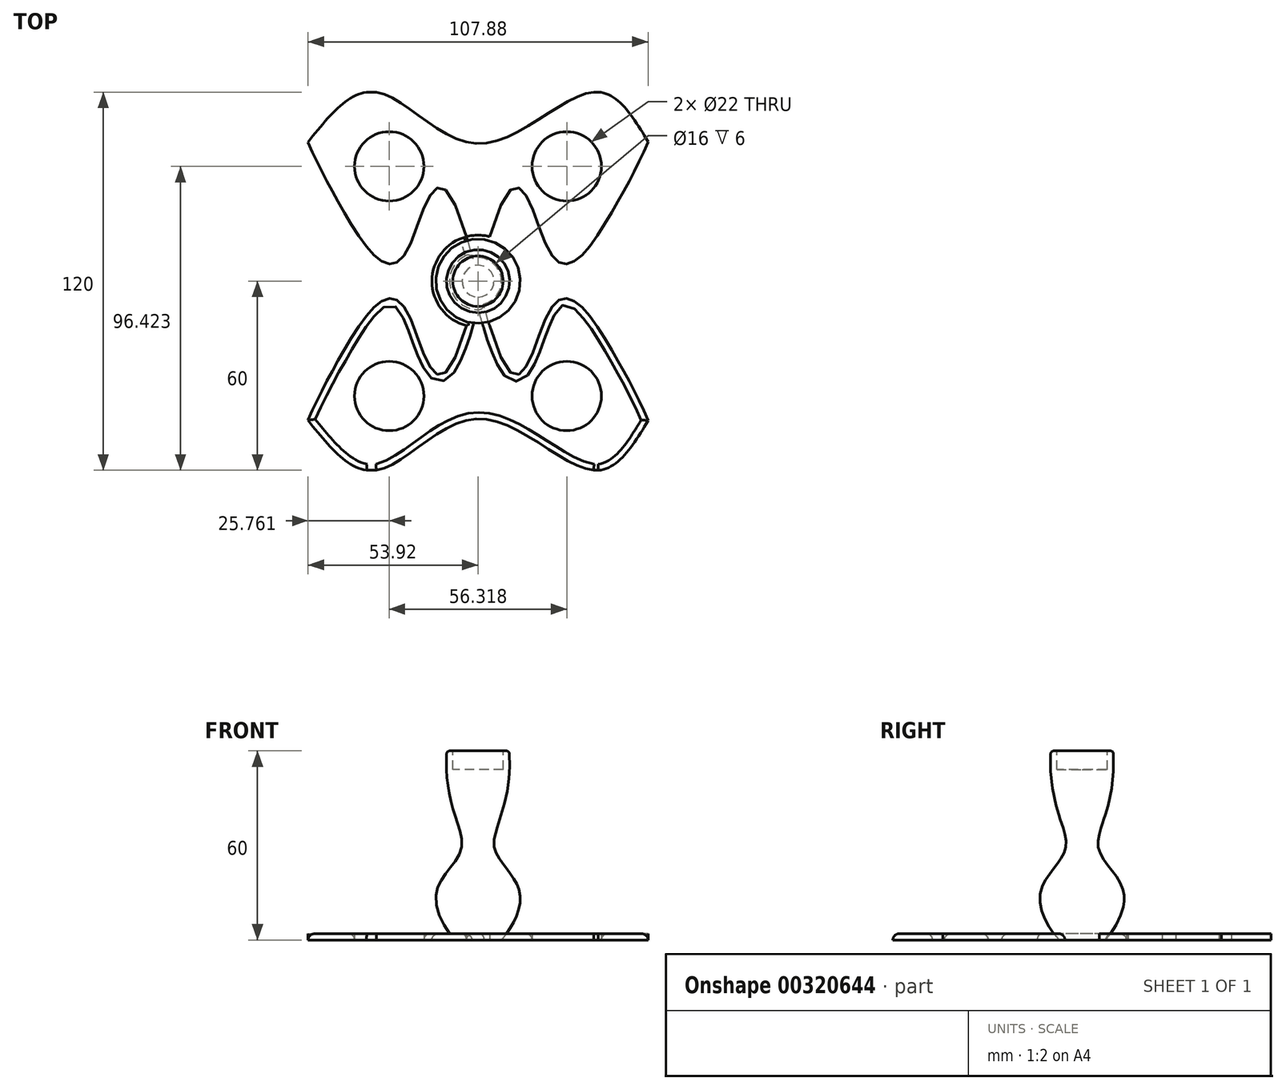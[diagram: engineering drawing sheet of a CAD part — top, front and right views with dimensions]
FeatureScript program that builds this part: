
annotation { "Feature Type Name" : "Feature", "Feature Type Description" : "" }
export const myFeature = defineFeature(function(context is Context, id is Id, definition is map)
    precondition{}
    {
        {
            var Q0;
            Q0=qCreatedBy(makeId("Top.planeOp"),FACE);
            var sketch = newSketch(context, id + "F0", { "sketchPlane" : qUnion([Q0])});
            skLineSegment(sketch, "E0.bottom", {"start": v(60, -60) * mm, "end": v(-60, -60) * mm});
            skLineSegment(sketch, "E0.top", {"start": v(60, 60) * mm, "end": v(-60, 60) * mm});
            skLineSegment(sketch, "E0.left", {"start": v(60, -60) * mm, "end": v(60, 60) * mm});
            skLineSegment(sketch, "E0.right", {"start": v(-60, -60) * mm, "end": v(-60, 60) * mm});
            skPoint(sketch, "E0.middle", {"position": v(0, 0) * mm});
            skCircle(sketch, "E1", {"center": v(-28.16, 36.42) * mm, "radius": 11 * mm});
            skCircle(sketch, "E2.MirrorC", {"center": v(28.16, 36.42) * mm, "radius": 11 * mm});
            skCircle(sketch, "E3.MirrorC", {"center": v(28.16, -36.42) * mm, "radius": 11 * mm});
            skCircle(sketch, "E4.MirrorC", {"center": v(-28.16, -36.42) * mm, "radius": 11 * mm});
            skFitSpline(sketch, "E5", {"points": [v(-60, 60) * mm, v(-42.49, 21.96) * mm, v(-22.78, 9.17) * mm, v(0, 0) * mm], "startDerivative": vector(42.96, -123.6) * mm, "endDerivative": vector(125.1, -535.95) * mm});
            skFitSpline(sketch, "E6.MirrorCS", {"points": [v(60, 60) * mm, v(42.49, 21.96) * mm, v(22.78, 9.17) * mm, v(0, 0) * mm], "startDerivative": vector(-42.96, -123.6) * mm, "endDerivative": vector(-125.1, -535.95) * mm});
            skFitSpline(sketch, "E7.MirrorCS", {"points": [v(-60, -60) * mm, v(-42.49, -21.96) * mm, v(-22.78, -9.17) * mm, v(0, 0) * mm], "startDerivative": vector(42.96, 123.6) * mm, "endDerivative": vector(125.1, 535.95) * mm});
            skFitSpline(sketch, "E8.MirrorCS", {"points": [v(60, -60) * mm, v(42.49, -21.96) * mm, v(22.78, -9.17) * mm, v(0, 0) * mm], "startDerivative": vector(-42.96, 123.6) * mm, "endDerivative": vector(-125.1, 535.95) * mm});
            skCircle(sketch, "E9", {"center": v(0, 0) * mm, "radius": 14.6 * mm});
            skFitSpline(sketch, "E10", {"points": [v(-54.3, -43.62) * mm, v(-32.24, -60) * mm, v(0, -43.62) * mm, v(36.74, -60) * mm, v(54.3, -43.62) * mm], "startDerivative": vector(89.76, -113.6) * mm, "endDerivative": vector(68.72, 116.74) * mm});
            skFitSpline(sketch, "E11.MirrorCS", {"points": [v(-54.3, 43.62) * mm, v(-32.24, 60) * mm, v(0, 43.62) * mm, v(36.74, 60) * mm, v(54.3, 43.62) * mm], "startDerivative": vector(89.76, 113.6) * mm, "endDerivative": vector(68.72, -116.74) * mm});
            skSolve(sketch);
        }
        {
            var Q0;
            {var subQ2=sQuery(id+"F0.wireOp",EDGE,"E7.MirrorCS");var subQ5=sQuery(id+"F0.wireOp",EDGE,"E8.MirrorCS");var subQ6=makeQuery(id+"F0.imprint","INTERSECT",VERTEX,{"derivedFrom":[subQ2,subQ5]});Q0=makeQuery(id+"F0.imprint","IMPRINT",FACE,{"disambiguationData":[TD([[makeQuery(id+"F0.imprint","IMPRINT",EDGE,{"disambiguationData":[TD([[subQ6,1.0]])],"derivedFrom":subQ2}),1.0]])]});}
            var Q1;
            {var subQ0=sQuery(id+"F0.wireOp",EDGE,"E8.MirrorCS");var subQ1=sQuery(id+"F0.wireOp",EDGE,"E7.MirrorCS");var subQ2=makeQuery(id+"F0.imprint","INTERSECT",VERTEX,{"derivedFrom":[subQ1,subQ0]});Q1=makeQuery(id+"F0.imprint","IMPRINT",FACE,{"disambiguationData":[TD([[makeQuery(id+"F0.imprint","IMPRINT",EDGE,{"disambiguationData":[TD([[subQ2,1.0]])],"derivedFrom":subQ1}),-1.0]])]});}
            var Q2;
            Q2=makeQuery(id+"F0.imprint","IMPRINT",FACE,{"disambiguationData":[TD([[makeQuery(id+"F0.imprint","IMPRINT",EDGE,{"derivedFrom":sQuery(id+"F0.wireOp",EDGE,"E1")}),-1.0]])]});
            var Q3;
            Q3=makeQuery(id+"F0.imprint","IMPRINT",FACE,{"disambiguationData":[TD([[makeQuery(id+"F0.imprint","IMPRINT",EDGE,{"derivedFrom":sQuery(id+"F0.wireOp",EDGE,"E3.MirrorC")}),-1.0]])]});
            extrude(context, id + "F1", {"entities" : qUnion([Q0, Q1, Q2, Q3]), "depth" : 2 * mm});
        }
        {
            var Q0;
            Q0=makeQuery(id+"F1.opExtrude","CAP_FACE",FACE,{"disambiguationData":[OSD([sQuery(id+"F0.wireOp",EDGE,"E0.bottom"),sQuery(id+"F0.wireOp",EDGE,"E0.top"),sQuery(id+"F0.wireOp",EDGE,"E1"),sQuery(id+"F0.wireOp",EDGE,"E2.MirrorC"),sQuery(id+"F0.wireOp",EDGE,"E3.MirrorC"),sQuery(id+"F0.wireOp",EDGE,"E4.MirrorC"),sQuery(id+"F0.wireOp",EDGE,"E5"),sQuery(id+"F0.wireOp",EDGE,"E6.MirrorCS"),sQuery(id+"F0.wireOp",EDGE,"E7.MirrorCS"),sQuery(id+"F0.wireOp",EDGE,"E8.MirrorCS"),sQuery(id+"F0.wireOp",EDGE,"E9")])],"isStart":false});
            fillet(context, id + "F2", {"entities" : qUnion([Q0]), "radius" : 2 * mm, "tangentPropagation" : true, "allowEdgeOverflow" : false});
        }
        {
            var Q0;
            Q0=qCreatedBy(makeId("Right.planeOp"),FACE);
            var sketch = newSketch(context, id + "F3", { "sketchPlane" : qUnion([Q0])});
            skLineSegment(sketch, "E12", {"start": v(-9.92, 60) * mm, "end": v(0, 60) * mm});
            skLineSegment(sketch, "E13", {"start": v(0, 60) * mm, "end": v(0, 0) * mm});
            skPoint(sketch, "E14", {"position": v(-4.96, 60) * mm});
            skPoint(sketch, "E15", {"position": v(-7.43, 0) * mm});
            skFitSpline(sketch, "E16", {"points": [v(-9.92, 60) * mm, v(-5.26, 28.95) * mm, v(-12.97, 16) * mm, v(-7.43, 0) * mm], "startDerivative": vector(-7.95, -133.58) * mm, "endDerivative": vector(42, -49.92) * mm});
            skLineSegment(sketch, "E17", {"start": v(0, 0) * mm, "end": v(-7.43, 0) * mm});
            skSolve(sketch);
        }
        {
            var Q0;
            Q0=qSketchRegion(id+"F3",true);
            var Q1;
            Q1=sQuery(id+"F3.wireOp",EDGE,"E13");
            revolve(context, id + "F4", {"operationType" : NewBodyOperationType.ADD, "entities" : qUnion([Q0]), "axis" : qUnion([Q1]), "revolveType" : RevolveType.FULL});
        }
        {
            var Q0;
            Q0=makeQuery(id+"F4.opRevolve","SWEPT_FACE",FACE,{"disambiguationData":[OSD([sQuery(id+"F3.wireOp",EDGE,"E12")])]});
            var sketch = newSketch(context, id + "F5", { "sketchPlane" : qUnion([Q0])});
            skCircle(sketch, "E18", {"center": v(0, 0) * mm, "radius": 8 * mm});
            skSolve(sketch);
        }
        {
            var Q0;
            Q0=qSketchRegion(id+"F5",true);
            extrude(context, id + "F6", {"entities" : qUnion([Q0]), "operationType" : NewBodyOperationType.REMOVE, "oppositeDirection" : true, "depth" : 6 * mm});
        }
        {
            var Q0;
            Q0=makeQuery(id+"F4.opRevolve","SWEPT_EDGE",EDGE,{"disambiguationData":[OSD([sQuery(id+"F3.wireOp",EDGE,"45efdf21-a1fe-441a-8c31-1d1d9af343b4"),sQuery(id+"F3.wireOp",EDGE,"E12")])]});
            var Q1;
            Q1=makeQuery(id+"F4.boolean.opBoolean","INTERSECT",EDGE,{"derivedFrom":[makeQuery(id+"F1.opExtrude","CAP_FACE",FACE,{"disambiguationData":[OSD([sQuery(id+"F0.wireOp",EDGE,"E0.bottom"),sQuery(id+"F0.wireOp",EDGE,"E0.top"),sQuery(id+"F0.wireOp",EDGE,"E1"),sQuery(id+"F0.wireOp",EDGE,"E2.MirrorC"),sQuery(id+"F0.wireOp",EDGE,"E3.MirrorC"),sQuery(id+"F0.wireOp",EDGE,"E4.MirrorC"),sQuery(id+"F0.wireOp",EDGE,"E5"),sQuery(id+"F0.wireOp",EDGE,"E6.MirrorCS"),sQuery(id+"F0.wireOp",EDGE,"E7.MirrorCS"),sQuery(id+"F0.wireOp",EDGE,"E8.MirrorCS"),sQuery(id+"F0.wireOp",EDGE,"E9"),sQuery(id+"F0.wireOp",EDGE,"E10"),sQuery(id+"F0.wireOp",EDGE,"E11.MirrorCS")])],"isStart":false}),makeQuery(id+"F4.opRevolve","SWEPT_FACE",FACE,{"disambiguationData":[OSD([sQuery(id+"F3.wireOp",EDGE,"45efdf21-a1fe-441a-8c31-1d1d9af343b4")])]})]});
            fillet(context, id + "F7", {"entities" : qUnion([Q0, Q1]), "radius" : 1 * mm, "tangentPropagation" : true, "allowEdgeOverflow" : false});
        }
    });
